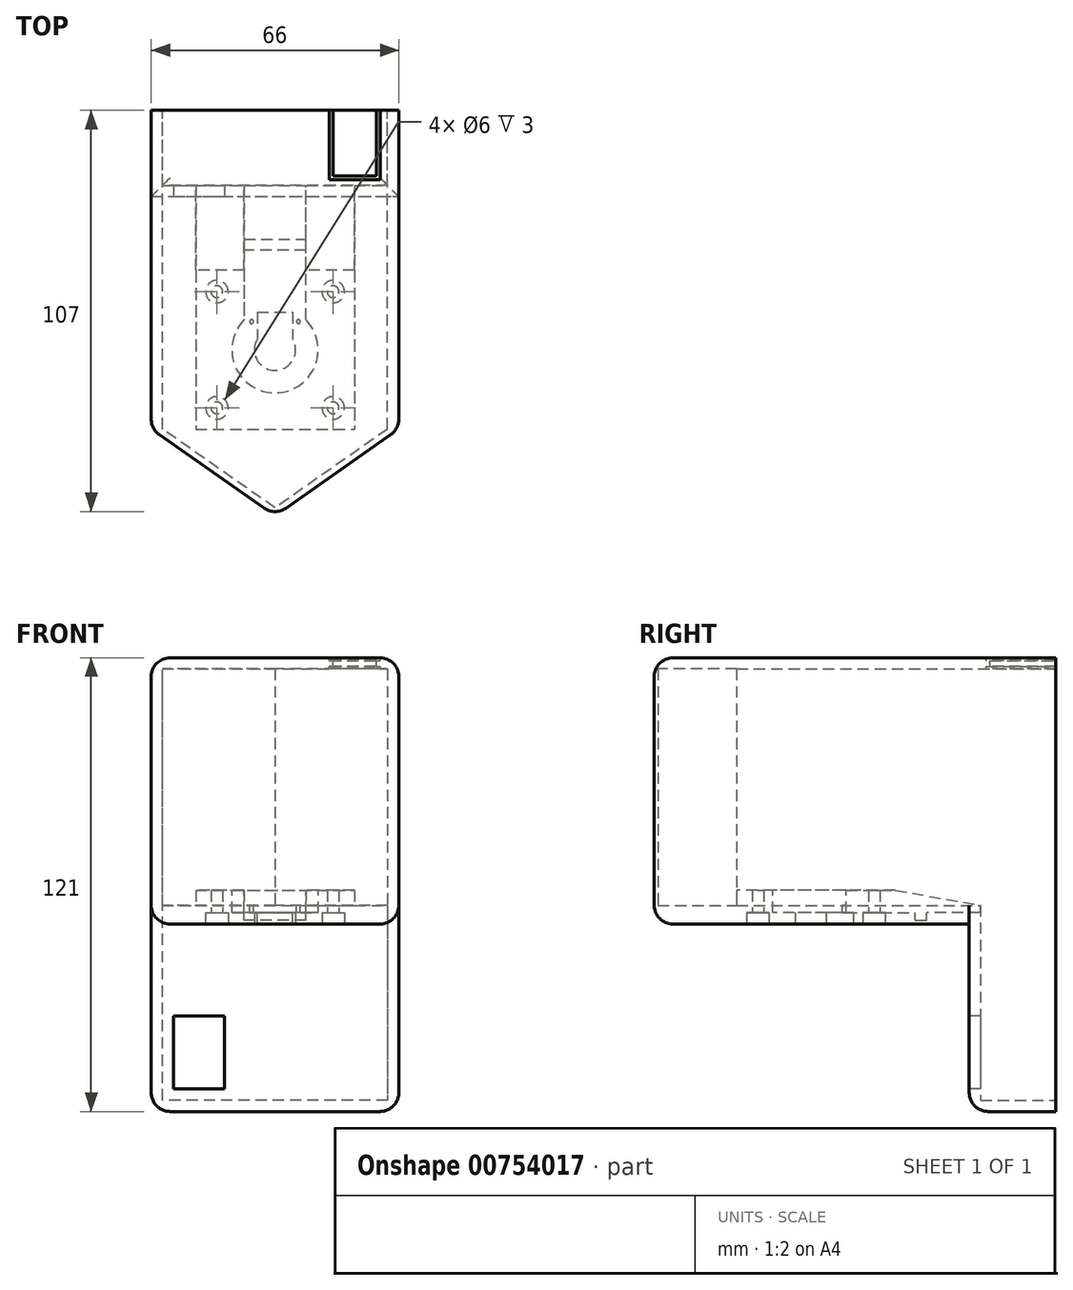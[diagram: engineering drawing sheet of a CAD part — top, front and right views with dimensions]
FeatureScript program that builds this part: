
annotation { "Feature Type Name" : "Feature", "Feature Type Description" : "" }
export const myFeature = defineFeature(function(context is Context, id is Id, definition is map)
    precondition{}
    {
        {
            var Q0;
            Q0=qCreatedBy(makeId("Front.planeOp"),FACE);
            var sketch = newSketch(context, id + "F0", { "sketchPlane" : qUnion([Q0])});
            skLineSegment(sketch, "E0", {"start": v(-33, -60.5) * mm, "end": v(33, -60.5) * mm});
            skLineSegment(sketch, "E1", {"start": v(33, -60.5) * mm, "end": v(33, 60.5) * mm});
            skLineSegment(sketch, "E2", {"start": v(33, 60.5) * mm, "end": v(-33, 60.5) * mm});
            skLineSegment(sketch, "E3", {"start": v(-33, 60.5) * mm, "end": v(-33, -60.5) * mm});
            skLineSegment(sketch, "E4", {"start": v(30, 57.5) * mm, "end": v(30, -57.5) * mm});
            skLineSegment(sketch, "E5", {"start": v(30, -57.5) * mm, "end": v(-30, -57.5) * mm});
            skLineSegment(sketch, "E6", {"start": v(-30, -57.5) * mm, "end": v(-30, 57.5) * mm});
            skLineSegment(sketch, "E7", {"start": v(-30, 57.5) * mm, "end": v(30, 57.5) * mm});
            skSolve(sketch);
        }
        {
            var Q0;
            Q0=makeQuery(id+"F0.imprint","IMPRINT",FACE,{"disambiguationData":[TD([[makeQuery(id+"F0.imprint","IMPRINT",EDGE,{"derivedFrom":sQuery(id+"F0.wireOp",EDGE,"E0")}),1.0]])]});
            extrude(context, id + "F1", {"entities" : qUnion([Q0]), "depth" : 20 * mm, "offsetDistance" : 25 * mm});
        }
        {
            var Q0;
            Q0=makeQuery(id+"F1.opExtrude","CAP_FACE",FACE,{"disambiguationData":[OSD([sQuery(id+"F0.wireOp",EDGE,"E0"),sQuery(id+"F0.wireOp",EDGE,"E1"),sQuery(id+"F0.wireOp",EDGE,"E2"),sQuery(id+"F0.wireOp",EDGE,"E3"),sQuery(id+"F0.wireOp",EDGE,"E4"),sQuery(id+"F0.wireOp",EDGE,"E5"),sQuery(id+"F0.wireOp",EDGE,"E6"),sQuery(id+"F0.wireOp",EDGE,"E7")])],"isStart":false});
            var sketch = newSketch(context, id + "F2", { "sketchPlane" : qUnion([Q0])});
            skLineSegment(sketch, "E8", {"start": v(-33, -10.5) * mm, "end": v(33, -10.5) * mm});
            skLineSegment(sketch, "E9", {"start": v(-33, -5.5) * mm, "end": v(33, -5.5) * mm});
            skSolve(sketch);
        }
        {
            var Q0;
            {var subQ5=makeQuery(id+"F1.opExtrude","CAP_EDGE",EDGE,{"disambiguationData":[OSD([sQuery(id+"F0.wireOp",EDGE,"E5")])],"isStart":false});Q0=makeQuery(id+"F2.imprint","IMPRINT",FACE,{"disambiguationData":[TD([[makeQuery(id+"F2.imprint","IMPRINT",EDGE,{"derivedFrom":subQ5}),-1.0]])]});}
            var Q1;
            {var subQ0=makeQuery(id+"F1.opExtrude","CAP_EDGE",EDGE,{"disambiguationData":[OSD([sQuery(id+"F0.wireOp",EDGE,"E0")])],"isStart":false});Q1=makeQuery(id+"F2.imprint","IMPRINT",FACE,{"disambiguationData":[TD([[makeQuery(id+"F2.imprint","IMPRINT",EDGE,{"derivedFrom":subQ0}),1.0]])]});}
            extrude(context, id + "F3", {"entities" : qUnion([Q0, Q1]), "operationType" : NewBodyOperationType.ADD, "depth" : 3 * mm, "offsetDistance" : 25 * mm});
        }
        {
            var Q0;
            {var subQ0=sQuery(id+"F2.wireOp",EDGE,"E8");var subQ1=makeQuery(id+"F1.opExtrude","CAP_EDGE",EDGE,{"disambiguationData":[OSD([sQuery(id+"F0.wireOp",EDGE,"E6")])],"isStart":false});var subQ2=makeQuery(id+"F2.imprint","INTERSECT",VERTEX,{"derivedFrom":[subQ1,subQ0]});Q0=makeQuery(id+"F2.imprint","IMPRINT",FACE,{"disambiguationData":[TD([[makeQuery(id+"F2.imprint","IMPRINT",EDGE,{"disambiguationData":[TD([[subQ2,-1.0]])],"derivedFrom":subQ0}),1.0]])]});}
            var Q1;
            {var subQ4=makeQuery(id+"F1.opExtrude","CAP_EDGE",EDGE,{"disambiguationData":[OSD([sQuery(id+"F0.wireOp",EDGE,"E2")])],"isStart":false});Q1=makeQuery(id+"F2.imprint","IMPRINT",FACE,{"disambiguationData":[TD([[makeQuery(id+"F2.imprint","IMPRINT",EDGE,{"derivedFrom":subQ4}),1.0]])]});}
            var Q2;
            {var subQ0=sQuery(id+"F2.wireOp",EDGE,"E8");var subQ1=makeQuery(id+"F1.opExtrude","CAP_EDGE",EDGE,{"disambiguationData":[OSD([sQuery(id+"F0.wireOp",EDGE,"E1")])],"isStart":false});var subQ2=makeQuery(id+"F2.imprint","INTERSECT",VERTEX,{"derivedFrom":[subQ1,subQ0]});Q2=makeQuery(id+"F2.imprint","IMPRINT",FACE,{"disambiguationData":[TD([[makeQuery(id+"F2.imprint","IMPRINT",EDGE,{"disambiguationData":[TD([[subQ2,1.0]])],"derivedFrom":subQ0}),1.0]])]});}
            var Q3;
            {var subQ0=sQuery(id+"F2.wireOp",EDGE,"E8");var subQ1=makeQuery(id+"F1.opExtrude","CAP_EDGE",EDGE,{"disambiguationData":[OSD([sQuery(id+"F0.wireOp",EDGE,"E3")])],"isStart":false});var subQ2=makeQuery(id+"F2.imprint","INTERSECT",VERTEX,{"derivedFrom":[subQ1,subQ0]});Q3=makeQuery(id+"F2.imprint","IMPRINT",FACE,{"disambiguationData":[TD([[makeQuery(id+"F2.imprint","IMPRINT",EDGE,{"disambiguationData":[TD([[subQ2,-1.0]])],"derivedFrom":subQ0}),1.0]])]});}
            extrude(context, id + "F4", {"entities" : qUnion([Q0, Q1, Q2, Q3]), "operationType" : NewBodyOperationType.ADD, "depth" : 65 * mm, "offsetDistance" : 25 * mm});
        }
        {
            var Q0;
            Q0=makeQuery(id+"F4.opExtrude","SWEPT_FACE",FACE,{"disambiguationData":[OSD([sQuery(id+"F2.wireOp",EDGE,"E8")])]});
            var sketch = newSketch(context, id + "F5", { "sketchPlane" : qUnion([Q0])});
            skCircle(sketch, "E10", {"center": v(0, 63.85) * mm, "radius": 5.5 * mm});
            skPoint(sketch, "E11", {"position": v(15.5, 79.35) * mm});
            skPoint(sketch, "E12", {"position": v(-15.5, 79.35) * mm});
            skPoint(sketch, "E13", {"position": v(-15.5, 48.35) * mm});
            skPoint(sketch, "E14", {"position": v(15.5, 48.35) * mm});
            skLineSegment(sketch, "E15.bottom", {"start": v(21.15, 42.7) * mm, "end": v(-21.15, 42.7) * mm, "construction": true});
            skLineSegment(sketch, "E15.top", {"start": v(21.15, 85) * mm, "end": v(-21.15, 85) * mm, "construction": true});
            skLineSegment(sketch, "E15.left", {"start": v(21.15, 42.7) * mm, "end": v(21.15, 85) * mm, "construction": true});
            skLineSegment(sketch, "E15.right", {"start": v(-21.15, 42.7) * mm, "end": v(-21.15, 85) * mm, "construction": true});
            skLineSegment(sketch, "E16", {"start": v(3.4, 63.85) * mm, "end": v(-2.9, 63.85) * mm, "construction": true});
            skSolve(sketch);
        }
        {
            var Q0;
            Q0=sQuery(id+"F5.wireOp",VERTEX,"E12");
            var Q1;
            Q1=sQuery(id+"F5.wireOp",VERTEX,"E13");
            var Q2;
            Q2=sQuery(id+"F5.wireOp",VERTEX,"E14");
            var Q3;
            Q3=sQuery(id+"F5.wireOp",VERTEX,"E11");
            var Q4;
            Q4=makeQuery(id+"F1.opExtrude","SWEPT_BODY",BODY,{"disambiguationData":[OSD([sQuery(id+"F0.wireOp",EDGE,"E0"),sQuery(id+"F0.wireOp",EDGE,"E1"),sQuery(id+"F0.wireOp",EDGE,"E2"),sQuery(id+"F0.wireOp",EDGE,"E3"),sQuery(id+"F0.wireOp",EDGE,"E4"),sQuery(id+"F0.wireOp",EDGE,"E5"),sQuery(id+"F0.wireOp",EDGE,"E6"),sQuery(id+"F0.wireOp",EDGE,"E7")])]});
            hole(context, id + "F6", {"style" : HoleStyle.C_BORE, "endStyle" : HoleEndStyle.BLIND, "holeDiameter" : 3.1 * mm, "cBoreDiameter" : 6 * mm, "cBoreDepth" : 3 * mm, "majorDiameter" : 5 * mm, "holeDepth" : 12 * mm, "isTappedThrough" : true, "tappedDepth" : 12 * mm, "tapClearance" : 3, "locations" : qUnion([Q0, Q1, Q2, Q3]), "scope" : qUnion([Q4])});
        }
        {
            var Q0;
            Q0=makeQuery(id+"F5.imprint","IMPRINT",FACE,{"disambiguationData":[TD([[makeQuery(id+"F5.imprint","IMPRINT",EDGE,{"derivedFrom":sQuery(id+"F5.wireOp",EDGE,"E10")}),1.0]])]});
            extrude(context, id + "F7", {"entities" : qUnion([Q0]), "operationType" : NewBodyOperationType.REMOVE, "oppositeDirection" : true, "depth" : 3 * mm, "offsetDistance" : 25 * mm});
        }
        {
            var Q0;
            Q0=makeQuery(id+"F3.opExtrude","CAP_FACE",FACE,{"disambiguationData":[OSD([sQuery(id+"F0.wireOp",EDGE,"E0"),sQuery(id+"F0.wireOp",EDGE,"E1"),sQuery(id+"F0.wireOp",EDGE,"E3"),sQuery(id+"F2.wireOp",EDGE,"E8")])],"isStart":false});
            var sketch = newSketch(context, id + "F8", { "sketchPlane" : qUnion([Q0])});
            skLineSegment(sketch, "E17.bottom", {"start": v(-27, -35) * mm, "end": v(-13.5, -35) * mm});
            skLineSegment(sketch, "E17.top", {"start": v(-27, -54.5) * mm, "end": v(-13.5, -54.5) * mm});
            skLineSegment(sketch, "E17.left", {"start": v(-27, -35) * mm, "end": v(-27, -54.5) * mm});
            skLineSegment(sketch, "E17.right", {"start": v(-13.5, -35) * mm, "end": v(-13.5, -54.5) * mm});
            skSolve(sketch);
        }
        {
            var Q0;
            Q0=makeQuery(id+"F8.imprint","IMPRINT",FACE,{"disambiguationData":[TD([[makeQuery(id+"F8.imprint","IMPRINT",EDGE,{"derivedFrom":sQuery(id+"F8.wireOp",EDGE,"E17.bottom")}),-1.0]])]});
            extrude(context, id + "F9", {"entities" : qUnion([Q0]), "operationType" : NewBodyOperationType.REMOVE, "oppositeDirection" : true, "depth" : 3 * mm, "offsetDistance" : 25 * mm});
        }
        {
            var Q0;
            {var subQ0=sQuery(id+"F0.wireOp",EDGE,"E2");Q0=makeQuery(id+"F4.boolean.opBoolean","MERGE",FACE,{"derivedFrom":[makeQuery(id+"F1.opExtrude","SWEPT_FACE",FACE,{"disambiguationData":[OSD([subQ0])]}),makeQuery(id+"F4.opExtrude","SWEPT_FACE",FACE,{"disambiguationData":[OSD([subQ0])]})]});}
            var sketch = newSketch(context, id + "F10", { "sketchPlane" : qUnion([Q0])});
            skLineSegment(sketch, "E18.bottom", {"start": v(28, -3) * mm, "end": v(14.5, -3) * mm});
            skLineSegment(sketch, "E18.top", {"start": v(28, -18.5) * mm, "end": v(14.5, -18.5) * mm});
            skLineSegment(sketch, "E18.left", {"start": v(28, -3) * mm, "end": v(28, -18.5) * mm});
            skLineSegment(sketch, "E18.right", {"start": v(14.5, -3) * mm, "end": v(14.5, -18.5) * mm});
            skSolve(sketch);
        }
        {
            var Q0;
            Q0=makeQuery(id+"F10.imprint","IMPRINT",FACE,{"disambiguationData":[TD([[makeQuery(id+"F10.imprint","IMPRINT",EDGE,{"derivedFrom":sQuery(id+"F10.wireOp",EDGE,"E18.bottom")}),1.0]])]});
            extrude(context, id + "F11", {"entities" : qUnion([Q0]), "operationType" : NewBodyOperationType.REMOVE, "oppositeDirection" : true, "depth" : 3 * mm, "offsetDistance" : 25 * mm});
        }
        {
            var Q0;
            Q0=makeQuery(id+"F4.opExtrude","SWEPT_FACE",FACE,{"disambiguationData":[OSD([sQuery(id+"F2.wireOp",EDGE,"E9")])]});
            var sketch = newSketch(context, id + "F12", { "sketchPlane" : qUnion([Q0])});
            skLineSegment(sketch, "E19", {"start": v(8.25, -55.84) * mm, "end": v(8.25, -20) * mm});
            skLineSegment(sketch, "E20", {"start": v(-8.25, -20) * mm, "end": v(-8.25, -55.84) * mm});
            skPoint(sketch, "E21", {"position": v(15.5, -48.35) * mm});
            skPoint(sketch, "E22", {"position": v(-15.5, -48.35) * mm});
            skCircle(sketch, "E23", {"center": v(0, -63.85) * mm, "radius": 11.5 * mm});
            skPoint(sketch, "E24", {"position": v(-6.25, -56.35) * mm});
            skPoint(sketch, "E25", {"position": v(6.25, -56.35) * mm});
            skCircle(sketch, "E26", {"center": v(6.25, -56.35) * mm, "radius": 0.5 * mm});
            skCircle(sketch, "E27", {"center": v(-6.25, -56.35) * mm, "radius": 0.5 * mm});
            skLineSegment(sketch, "E28", {"start": v(-8.25, -55.84) * mm, "end": v(-8.25, -58.35) * mm, "construction": true});
            skLineSegment(sketch, "E29", {"start": v(-8.25, -58.35) * mm, "end": v(-4.75, -58.35) * mm, "construction": true});
            skLineSegment(sketch, "E30", {"start": v(-4.75, -53.85) * mm, "end": v(4.75, -53.85) * mm});
            skLineSegment(sketch, "E31", {"start": v(4.75, -58.35) * mm, "end": v(8.25, -58.35) * mm, "construction": true});
            skLineSegment(sketch, "E32", {"start": v(8.25, -58.35) * mm, "end": v(8.25, -55.84) * mm, "construction": true});
            skCircle(sketch, "E33", {"center": v(0, -63.85) * mm, "radius": 5.5 * mm});
            skLineSegment(sketch, "E34", {"start": v(4.75, -53.85) * mm, "end": v(4.75, -61.08) * mm});
            skLineSegment(sketch, "E35", {"start": v(-4.75, -53.85) * mm, "end": v(-4.75, -61.08) * mm});
            skLineSegment(sketch, "E36.bottom", {"start": v(21.15, -42.7) * mm, "end": v(-21.15, -42.7) * mm});
            skLineSegment(sketch, "E36.top", {"start": v(21.15, -85) * mm, "end": v(-21.15, -85) * mm});
            skLineSegment(sketch, "E36.left", {"start": v(21.15, -42.7) * mm, "end": v(21.15, -85) * mm});
            skLineSegment(sketch, "E36.right", {"start": v(-21.15, -42.7) * mm, "end": v(-21.15, -85) * mm});
            skSolve(sketch);
        }
        {
            var Q0;
            Q0=makeQuery(id+"F12.imprint","IMPRINT",FACE,{"disambiguationData":[TD([[makeQuery(id+"F12.imprint","IMPRINT",EDGE,{"derivedFrom":sQuery(id+"F12.wireOp",EDGE,"E23")}),1.0]])]});
            var Q1;
            {var subQ0=sQuery(id+"F12.wireOp",EDGE,"E19");var subQ1=makeQuery(id+"F4.opExtrude","CAP_EDGE",EDGE,{"disambiguationData":[OSD([sQuery(id+"F2.wireOp",EDGE,"E9")])],"isStart":true});var subQ2=makeQuery(id+"F12.imprint","INTERSECT",VERTEX,{"derivedFrom":[subQ1,subQ0]});Q1=makeQuery(id+"F12.imprint","IMPRINT",FACE,{"disambiguationData":[TD([[makeQuery(id+"F12.imprint","IMPRINT",EDGE,{"disambiguationData":[TD([[subQ2,1.0]])],"derivedFrom":subQ0}),1.0]])]});}
            var Q2;
            {var subQ0=sQuery(id+"F12.wireOp",EDGE,"t75Lk9a1-lg42-faZ2-Xwdc-VcRS5GfcYv8D");var subQ1=sQuery(id+"F12.wireOp",EDGE,"E23");var subQ2=makeQuery(id+"F12.imprint","INTERSECT",VERTEX,{"derivedFrom":[subQ1,subQ0]});Q2=makeQuery(id+"F12.imprint","IMPRINT",FACE,{"disambiguationData":[TD([[makeQuery(id+"F12.imprint","IMPRINT",EDGE,{"disambiguationData":[TD([[subQ2,-1.0]])],"derivedFrom":subQ1}),-1.0]])]});}
            var Q3;
            {var subQ0=sQuery(id+"F12.wireOp",EDGE,"E30");var subQ1=sQuery(id+"F12.wireOp",EDGE,"E23");var subQ2=makeQuery(id+"F12.imprint","INTERSECT",VERTEX,{"disambiguationData":[OD(0.0)],"derivedFrom":[subQ1,subQ0]});Q3=makeQuery(id+"F12.imprint","IMPRINT",FACE,{"disambiguationData":[TD([[makeQuery(id+"F12.imprint","IMPRINT",EDGE,{"disambiguationData":[TD([[subQ2,-1.0]])],"derivedFrom":subQ1}),1.0]])]});}
            var Q4;
            {var subQ0=sQuery(id+"F12.wireOp",EDGE,"E33");var subQ1=makeQuery(id+"F12.imprint","INTERSECT",VERTEX,{"derivedFrom":[subQ0,sQuery(id+"F12.wireOp",EDGE,"E34")]});Q4=makeQuery(id+"F12.imprint","IMPRINT",FACE,{"disambiguationData":[TD([[makeQuery(id+"F12.imprint","IMPRINT",EDGE,{"disambiguationData":[TD([[subQ1,-1.0]])],"derivedFrom":subQ0}),1.0]])]});}
            extrude(context, id + "F13", {"entities" : qUnion([Q0, Q1, Q2, Q3, Q4]), "operationType" : NewBodyOperationType.REMOVE, "oppositeDirection" : true, "depth" : 2 * mm, "offsetDistance" : 25 * mm});
        }
        {
            var Q0;
            Q0=makeQuery(id+"F12.imprint","IMPRINT",FACE,{"disambiguationData":[TD([[makeQuery(id+"F12.imprint","IMPRINT",EDGE,{"derivedFrom":sQuery(id+"F12.wireOp",EDGE,"E30")}),-1.0]])]});
            extrude(context, id + "F14", {"entities" : qUnion([Q0]), "operationType" : NewBodyOperationType.REMOVE, "oppositeDirection" : true, "depth" : 25 * mm, "offsetDistance" : 25 * mm});
        }
        {
            var Q0;
            Q0=makeQuery(id+"F13.boolean.opBoolean","COPY",FACE,{"derivedFrom":makeQuery(id+"F13.opExtrude","CAP_FACE",FACE,{"disambiguationData":[OSD([sQuery(id+"F2.wireOp",EDGE,"E9"),sQuery(id+"F12.wireOp",EDGE,"E19"),sQuery(id+"F12.wireOp",EDGE,"E20"),sQuery(id+"F12.wireOp",EDGE,"E23"),sQuery(id+"F12.wireOp",EDGE,"E26"),sQuery(id+"F12.wireOp",EDGE,"E27"),sQuery(id+"F12.wireOp",EDGE,"E30"),sQuery(id+"F12.wireOp",EDGE,"E33"),sQuery(id+"F12.wireOp",EDGE,"E34"),sQuery(id+"F12.wireOp",EDGE,"E35")])],"isStart":false})});
            var sketch = newSketch(context, id + "F15", { "sketchPlane" : qUnion([Q0])});
            skLineSegment(sketch, "E37", {"start": v(8.25, -37.35) * mm, "end": v(-8.25, -37.35) * mm});
            skLineSegment(sketch, "E38", {"start": v(-8.25, -34.35) * mm, "end": v(8.25, -34.35) * mm});
            skLineSegment(sketch, "E39", {"start": v(-8.25, -34.35) * mm, "end": v(-8.25, -37.35) * mm});
            skLineSegment(sketch, "E40", {"start": v(8.25, -34.35) * mm, "end": v(8.25, -37.35) * mm});
            skSolve(sketch);
        }
        {
            var Q0;
            Q0=makeQuery(id+"F15.imprint","IMPRINT",FACE,{"disambiguationData":[TD([[makeQuery(id+"F15.imprint","IMPRINT",EDGE,{"derivedFrom":sQuery(id+"F15.wireOp",EDGE,"E37")}),-1.0]])]});
            extrude(context, id + "F16", {"entities" : qUnion([Q0]), "operationType" : NewBodyOperationType.REMOVE, "oppositeDirection" : true, "depth" : 2 * mm, "offsetDistance" : 25 * mm});
        }
        {
            var Q0;
            Q0=makeQuery(id+"F4.opExtrude","SWEPT_FACE",FACE,{"disambiguationData":[OSD([sQuery(id+"F2.wireOp",EDGE,"E8")])]});
            var sketch = newSketch(context, id + "F17", { "sketchPlane" : qUnion([Q0])});
            skLineSegment(sketch, "E41", {"start": v(0, 108.1) * mm, "end": v(-33, 85) * mm});
            skPoint(sketch, "E41.startSnap0", {"position": v(0, 85) * mm});
            skLineSegment(sketch, "E42", {"start": v(0, 108.1) * mm, "end": v(33, 85) * mm});
            skSolve(sketch);
        }
        {
            var Q0;
            Q0=makeQuery(id+"F17.imprint","IMPRINT",FACE,{"disambiguationData":[TD([[makeQuery(id+"F17.imprint","IMPRINT",EDGE,{"derivedFrom":sQuery(id+"F17.wireOp",EDGE,"E41")}),1.0]])]});
            extrude(context, id + "F18", {"entities" : qUnion([Q0]), "operationType" : NewBodyOperationType.ADD, "oppositeDirection" : true, "depth" : 5 * mm, "offsetDistance" : 25 * mm});
        }
        {
            var Q0;
            {var subQ0=sQuery(id+"F2.wireOp",EDGE,"E8");var subQ2=sQuery(id+"F2.wireOp",EDGE,"E9");var subQ4=sQuery(id+"F0.wireOp",EDGE,"E4");Q0=makeQuery(id+"F18.boolean.opBoolean","MERGE",FACE,{"derivedFrom":[makeQuery(id+"F13.boolean.opBoolean","SPLIT",FACE,{"disambiguationData":[TD([makeQuery(id+"F1.opExtrude","SWEPT_FACE",FACE,{"disambiguationData":[OSD([subQ4])]})])],"derivedFrom":makeQuery(id+"F4.opExtrude","SWEPT_FACE",FACE,{"disambiguationData":[OSD([subQ2])]})}),makeQuery(id+"F18.opExtrude","CAP_FACE",FACE,{"disambiguationData":[OSD([subQ0,sQuery(id+"F17.wireOp",EDGE,"E41"),sQuery(id+"F17.wireOp",EDGE,"E42")])],"isStart":false})]});}
            var sketch = newSketch(context, id + "F19", { "sketchPlane" : qUnion([Q0])});
            skLineSegment(sketch, "E43", {"start": v(30, -85) * mm, "end": v(0, -106) * mm});
            skLineSegment(sketch, "E44", {"start": v(0, -106) * mm, "end": v(-30, -85) * mm});
            skSolve(sketch);
        }
        {
            var Q0;
            {var subQ0=sQuery(id+"F0.wireOp",EDGE,"E2");Q0=makeQuery(id+"F4.boolean.opBoolean","MERGE",FACE,{"derivedFrom":[makeQuery(id+"F1.opExtrude","SWEPT_FACE",FACE,{"disambiguationData":[OSD([subQ0])]}),makeQuery(id+"F4.opExtrude","SWEPT_FACE",FACE,{"disambiguationData":[OSD([subQ0])]})]});}
            var sketch = newSketch(context, id + "F20", { "sketchPlane" : qUnion([Q0])});
            skLineSegment(sketch, "E45", {"start": v(33, -85) * mm, "end": v(0, -108.1) * mm});
            skLineSegment(sketch, "E46", {"start": v(0, -108.1) * mm, "end": v(-33, -85) * mm});
            skSolve(sketch);
        }
        {
            var Q0;
            Q0=makeQuery(id+"F20.imprint","IMPRINT",FACE,{"disambiguationData":[TD([[makeQuery(id+"F20.imprint","IMPRINT",EDGE,{"derivedFrom":sQuery(id+"F20.wireOp",EDGE,"E45")}),-1.0]])]});
            extrude(context, id + "F21", {"entities" : qUnion([Q0]), "operationType" : NewBodyOperationType.ADD, "oppositeDirection" : true, "depth" : 3 * mm, "offsetDistance" : 25 * mm});
        }
        {
            var Q0;
            Q0=makeQuery(id+"F19.imprint","IMPRINT",FACE,{"disambiguationData":[TD([[makeQuery(id+"F19.imprint","IMPRINT",EDGE,{"derivedFrom":sQuery(id+"F19.wireOp",EDGE,"E43")}),1.0]])]});
            extrude(context, id + "F22", {"entities" : qUnion([Q0]), "operationType" : NewBodyOperationType.ADD, "depth" : 63 * mm, "offsetDistance" : 25 * mm});
        }
        {
            var Q0;
            Q0=makeQuery(id+"F18.opExtrude","CAP_EDGE",EDGE,{"disambiguationData":[OSD([sQuery(id+"F17.wireOp",EDGE,"E42")])],"isStart":true});
            var Q1;
            Q1=makeQuery(id+"F18.opExtrude","CAP_EDGE",EDGE,{"disambiguationData":[OSD([sQuery(id+"F17.wireOp",EDGE,"E41")])],"isStart":true});
            var Q2;
            {var subQ0=sQuery(id+"F17.wireOp",EDGE,"E42");var subQ1=sQuery(id+"F17.wireOp",EDGE,"E41");Q2=makeQuery(id+"F22.boolean.opBoolean","MERGE",EDGE,{"derivedFrom":[makeQuery(id+"F18.opExtrude","SWEPT_EDGE",EDGE,{"disambiguationData":[OSD([subQ1,subQ0])]}),makeQuery(id+"F21.opExtrude","SWEPT_EDGE",EDGE,{"disambiguationData":[OSD([sQuery(id+"F20.wireOp",EDGE,"E45"),sQuery(id+"F20.wireOp",EDGE,"E46")])]}),makeQuery(id+"F22.opExtrude","SWEPT_EDGE",EDGE,{"disambiguationData":[OSD([subQ1,subQ0])]})]});}
            var Q3;
            Q3=makeQuery(id+"F3.opExtrude","CAP_EDGE",EDGE,{"disambiguationData":[OSD([sQuery(id+"F2.wireOp",EDGE,"E8")])],"isStart":false});
            var Q4;
            Q4=makeQuery(id+"F4.opExtrude","SWEPT_EDGE",EDGE,{"disambiguationData":[OSD([sQuery(id+"F0.wireOp",EDGE,"E1"),sQuery(id+"F2.wireOp",EDGE,"E8")])]});
            var Q5;
            {var subQ0=sQuery(id+"F17.wireOp",EDGE,"E42");var subQ1=sQuery(id+"F2.wireOp",EDGE,"E8");var subQ2=sQuery(id+"F0.wireOp",EDGE,"E1");var subQ3=makeQuery(id+"F4.opExtrude","CAP_EDGE",EDGE,{"disambiguationData":[OSD([subQ2])],"isStart":false});var subQ4=makeQuery(id+"F18.boolean.opBoolean","SPLIT",EDGE,{"derivedFrom":subQ3});Q5=makeQuery(id+"F22.boolean.opBoolean","MERGE",EDGE,{"derivedFrom":[makeQuery(id+"F18.boolean.opBoolean","MERGE",EDGE,{"derivedFrom":[subQ3,makeQuery(id+"F18.opExtrude","SWEPT_EDGE",EDGE,{"disambiguationData":[OSD([subQ2,subQ1,subQ0])]})]}),makeQuery(id+"F21.boolean.opBoolean","MERGE",EDGE,{"derivedFrom":[subQ4,makeQuery(id+"F21.opExtrude","SWEPT_EDGE",EDGE,{"disambiguationData":[OSD([subQ2,sQuery(id+"F0.wireOp",EDGE,"E2"),sQuery(id+"F20.wireOp",EDGE,"E45")])]})]}),makeQuery(id+"F21.boolean.opBoolean","SPLIT",EDGE,{"derivedFrom":subQ4}),makeQuery(id+"F22.opExtrude","SWEPT_EDGE",EDGE,{"disambiguationData":[OSD([subQ1,subQ0])]})]});}
            var Q6;
            Q6=makeQuery(id+"F4.opExtrude","SWEPT_EDGE",EDGE,{"disambiguationData":[OSD([sQuery(id+"F0.wireOp",EDGE,"E3"),sQuery(id+"F2.wireOp",EDGE,"E8")])]});
            var Q7;
            {var subQ0=sQuery(id+"F17.wireOp",EDGE,"E41");var subQ1=sQuery(id+"F2.wireOp",EDGE,"E8");var subQ2=sQuery(id+"F0.wireOp",EDGE,"E3");var subQ3=makeQuery(id+"F4.opExtrude","CAP_EDGE",EDGE,{"disambiguationData":[OSD([subQ2])],"isStart":false});var subQ4=makeQuery(id+"F18.boolean.opBoolean","SPLIT",EDGE,{"derivedFrom":subQ3});Q7=makeQuery(id+"F22.boolean.opBoolean","MERGE",EDGE,{"derivedFrom":[makeQuery(id+"F18.boolean.opBoolean","MERGE",EDGE,{"derivedFrom":[subQ3,makeQuery(id+"F18.opExtrude","SWEPT_EDGE",EDGE,{"disambiguationData":[OSD([subQ2,subQ1,subQ0])]})]}),makeQuery(id+"F21.boolean.opBoolean","MERGE",EDGE,{"derivedFrom":[subQ4,makeQuery(id+"F21.opExtrude","SWEPT_EDGE",EDGE,{"disambiguationData":[OSD([sQuery(id+"F0.wireOp",EDGE,"E2"),subQ2,sQuery(id+"F20.wireOp",EDGE,"E46")])]})]}),makeQuery(id+"F21.boolean.opBoolean","SPLIT",EDGE,{"derivedFrom":subQ4}),makeQuery(id+"F22.opExtrude","SWEPT_EDGE",EDGE,{"disambiguationData":[OSD([subQ1,subQ0])]})]});}
            var Q8;
            Q8=makeQuery(id+"F21.opExtrude","CAP_EDGE",EDGE,{"disambiguationData":[OSD([sQuery(id+"F20.wireOp",EDGE,"E46")])],"isStart":true});
            var Q9;
            {var subQ0=sQuery(id+"F0.wireOp",EDGE,"E3");var subQ1=sQuery(id+"F0.wireOp",EDGE,"E2");Q9=makeQuery(id+"F4.boolean.opBoolean","MERGE",EDGE,{"derivedFrom":[makeQuery(id+"F1.opExtrude","SWEPT_EDGE",EDGE,{"disambiguationData":[OSD([subQ1,subQ0])]}),makeQuery(id+"F4.opExtrude","SWEPT_EDGE",EDGE,{"disambiguationData":[OSD([subQ1,subQ0])]})]});}
            var Q10;
            {var subQ0=sQuery(id+"F0.wireOp",EDGE,"E2");var subQ1=sQuery(id+"F0.wireOp",EDGE,"E1");Q10=makeQuery(id+"F4.boolean.opBoolean","MERGE",EDGE,{"derivedFrom":[makeQuery(id+"F1.opExtrude","SWEPT_EDGE",EDGE,{"disambiguationData":[OSD([subQ1,subQ0])]}),makeQuery(id+"F4.opExtrude","SWEPT_EDGE",EDGE,{"disambiguationData":[OSD([subQ1,subQ0])]})]});}
            var Q11;
            Q11=makeQuery(id+"F3.opExtrude","CAP_EDGE",EDGE,{"disambiguationData":[OSD([sQuery(id+"F0.wireOp",EDGE,"E0")])],"isStart":false});
            var Q12;
            {var subQ0=sQuery(id+"F0.wireOp",EDGE,"E3");var subQ1=sQuery(id+"F0.wireOp",EDGE,"E0");Q12=makeQuery(id+"F3.boolean.opBoolean","MERGE",EDGE,{"derivedFrom":[makeQuery(id+"F1.opExtrude","SWEPT_EDGE",EDGE,{"disambiguationData":[OSD([subQ1,subQ0])]}),makeQuery(id+"F3.opExtrude","SWEPT_EDGE",EDGE,{"disambiguationData":[OSD([subQ1,subQ0])]})]});}
            var Q13;
            {var subQ0=sQuery(id+"F0.wireOp",EDGE,"E1");var subQ1=sQuery(id+"F0.wireOp",EDGE,"E0");Q13=makeQuery(id+"F3.boolean.opBoolean","MERGE",EDGE,{"derivedFrom":[makeQuery(id+"F1.opExtrude","SWEPT_EDGE",EDGE,{"disambiguationData":[OSD([subQ1,subQ0])]}),makeQuery(id+"F3.opExtrude","SWEPT_EDGE",EDGE,{"disambiguationData":[OSD([subQ1,subQ0])]})]});}
            var Q14;
            Q14=makeQuery(id+"F21.opExtrude","CAP_EDGE",EDGE,{"disambiguationData":[OSD([sQuery(id+"F20.wireOp",EDGE,"E45")])],"isStart":true});
            fillet(context, id + "F23", {"entities" : qUnion([Q0, Q1, Q2, Q3, Q4, Q5, Q6, Q7, Q8, Q9, Q10, Q11, Q12, Q13, Q14]), "radius" : 5 * mm, "tangentPropagation" : true, "allowEdgeOverflow" : false});
        }
        {
            var Q0;
            Q0=makeQuery(id+"F12.imprint","IMPRINT",FACE,{"disambiguationData":[TD([[makeQuery(id+"F12.imprint","IMPRINT",EDGE,{"derivedFrom":sQuery(id+"F12.wireOp",EDGE,"E36.top")}),1.0]])]});
            extrude(context, id + "F24", {"entities" : qUnion([Q0]), "operationType" : NewBodyOperationType.ADD, "depth" : 4 * mm, "offsetDistance" : 25 * mm});
        }
        {
            var Q0;
            {var subQ0=sQuery(id+"F12.wireOp",EDGE,"E19");Q0=makeQuery(id+"F24.boolean.opBoolean","MERGE",FACE,{"derivedFrom":[makeQuery(id+"F16.boolean.opBoolean","MERGE",FACE,{"derivedFrom":[makeQuery(id+"F13.boolean.opBoolean","COPY",FACE,{"derivedFrom":makeQuery(id+"F13.opExtrude","SWEPT_FACE",FACE,{"disambiguationData":[OSD([subQ0])]})}),makeQuery(id+"F16.opExtrude","SWEPT_FACE",FACE,{"disambiguationData":[OSD([sQuery(id+"F15.wireOp",EDGE,"E40")])]})]}),makeQuery(id+"F24.opExtrude","SWEPT_FACE",FACE,{"disambiguationData":[OSD([subQ0])]})]});}
            var sketch = newSketch(context, id + "F25", { "sketchPlane" : qUnion([Q0])});
            skLineSegment(sketch, "E47", {"start": v(42.7, -1.5) * mm, "end": v(20, -5.5) * mm});
            skSolve(sketch);
        }
        {
            var Q0;
            Q0=makeQuery(id+"F25.imprint","IMPRINT",FACE,{"disambiguationData":[TD([[makeQuery(id+"F25.imprint","IMPRINT",EDGE,{"derivedFrom":sQuery(id+"F25.wireOp",EDGE,"E47")}),1.0]])]});
            extrude(context, id + "F26", {"entities" : qUnion([Q0]), "operationType" : NewBodyOperationType.ADD, "oppositeDirection" : true, "depth" : 12.9 * mm, "offsetDistance" : 25 * mm});
        }
        {
            var Q0;
            {var subQ0=sQuery(id+"F12.wireOp",EDGE,"E20");Q0=makeQuery(id+"F24.boolean.opBoolean","MERGE",FACE,{"derivedFrom":[makeQuery(id+"F16.boolean.opBoolean","MERGE",FACE,{"derivedFrom":[makeQuery(id+"F13.boolean.opBoolean","COPY",FACE,{"derivedFrom":makeQuery(id+"F13.opExtrude","SWEPT_FACE",FACE,{"disambiguationData":[OSD([subQ0])]})}),makeQuery(id+"F16.opExtrude","SWEPT_FACE",FACE,{"disambiguationData":[OSD([sQuery(id+"F15.wireOp",EDGE,"E39")])]})]}),makeQuery(id+"F24.opExtrude","SWEPT_FACE",FACE,{"disambiguationData":[OSD([subQ0])]})]});}
            var sketch = newSketch(context, id + "F27", { "sketchPlane" : qUnion([Q0])});
            skLineSegment(sketch, "E48", {"start": v(-42.7, -1.5) * mm, "end": v(-20, -5.5) * mm});
            skSolve(sketch);
        }
        {
            var Q0;
            Q0=makeQuery(id+"F27.imprint","IMPRINT",FACE,{"disambiguationData":[TD([[makeQuery(id+"F27.imprint","IMPRINT",EDGE,{"derivedFrom":sQuery(id+"F27.wireOp",EDGE,"E48")}),-1.0]])]});
            extrude(context, id + "F28", {"entities" : qUnion([Q0]), "operationType" : NewBodyOperationType.ADD, "oppositeDirection" : true, "depth" : 12.9 * mm, "offsetDistance" : 25 * mm});
        }
        {
            var Q0;
            Q0=makeQuery(id+"F11.boolean.opBoolean","COPY",FACE,{"derivedFrom":makeQuery(id+"F11.opExtrude","SWEPT_FACE",FACE,{"disambiguationData":[OSD([sQuery(id+"F10.wireOp",EDGE,"E18.left")])]})});
            var sketch = newSketch(context, id + "F29", { "sketchPlane" : qUnion([Q0])});
            skLineSegment(sketch, "E49", {"start": v(18.5, 59.75) * mm, "end": v(3, 59.75) * mm});
            skPoint(sketch, "E49.endSnap0", {"position": v(3, 59) * mm});
            skLineSegment(sketch, "E50", {"start": v(3, 58.25) * mm, "end": v(18.5, 58.25) * mm});
            skLineSegment(sketch, "E51", {"start": v(18.5, 59) * mm, "end": v(3, 59) * mm, "construction": true});
            skSolve(sketch);
        }
        {
            var Q0;
            {var subQ0=sQuery(id+"F29.wireOp",EDGE,"E49");Q0=makeQuery(id+"F29.imprint","IMPRINT",FACE,{"disambiguationData":[TD([[makeQuery(id+"F29.imprint","IMPRINT",EDGE,{"derivedFrom":subQ0}),1.0]])]});}
            extrude(context, id + "F30", {"entities" : qUnion([Q0]), "operationType" : NewBodyOperationType.ADD, "depth" : 1 * mm, "offsetDistance" : 25 * mm});
        }
        {
            var Q0;
            Q0=makeQuery(id+"F11.boolean.opBoolean","COPY",FACE,{"derivedFrom":makeQuery(id+"F11.opExtrude","SWEPT_FACE",FACE,{"disambiguationData":[OSD([sQuery(id+"F10.wireOp",EDGE,"E18.right")])]})});
            var sketch = newSketch(context, id + "F31", { "sketchPlane" : qUnion([Q0])});
            skLineSegment(sketch, "E52", {"start": v(-18.5, 59) * mm, "end": v(-3, 59) * mm, "construction": true});
            skLineSegment(sketch, "E53", {"start": v(-3, 59.75) * mm, "end": v(-18.5, 59.75) * mm});
            skLineSegment(sketch, "E54", {"start": v(-18.5, 58.25) * mm, "end": v(-3, 58.25) * mm});
            skSolve(sketch);
        }
        {
            var Q0;
            {var subQ0=sQuery(id+"F31.wireOp",EDGE,"E53");Q0=makeQuery(id+"F31.imprint","IMPRINT",FACE,{"disambiguationData":[TD([[makeQuery(id+"F31.imprint","IMPRINT",EDGE,{"derivedFrom":subQ0}),1.0]])]});}
            extrude(context, id + "F32", {"entities" : qUnion([Q0]), "operationType" : NewBodyOperationType.ADD, "depth" : 1 * mm, "offsetDistance" : 25 * mm});
        }
        {
            var Q0;
            Q0=makeQuery(id+"F11.boolean.opBoolean","COPY",FACE,{"derivedFrom":makeQuery(id+"F11.opExtrude","SWEPT_FACE",FACE,{"disambiguationData":[OSD([sQuery(id+"F10.wireOp",EDGE,"E18.top")])]})});
            var sketch = newSketch(context, id + "F33", { "sketchPlane" : qUnion([Q0])});
            skLineSegment(sketch, "E55", {"start": v(-27, 59.75) * mm, "end": v(-15.5, 59.75) * mm});
            skLineSegment(sketch, "E56", {"start": v(-27, 58.25) * mm, "end": v(-15.5, 58.25) * mm});
            skSolve(sketch);
        }
        {
            var Q0;
            Q0=makeQuery(id+"F33.imprint","IMPRINT",FACE,{"disambiguationData":[TD([[makeQuery(id+"F33.imprint","IMPRINT",EDGE,{"derivedFrom":sQuery(id+"F33.wireOp",EDGE,"E55")}),-1.0]])]});
            extrude(context, id + "F34", {"entities" : qUnion([Q0]), "operationType" : NewBodyOperationType.ADD, "depth" : 1 * mm, "offsetDistance" : 25 * mm});
        }
        {
            var Q0;
            Q0=makeQuery(id+"F11.boolean.opBoolean","COPY",FACE,{"derivedFrom":makeQuery(id+"F11.opExtrude","SWEPT_FACE",FACE,{"disambiguationData":[OSD([sQuery(id+"F10.wireOp",EDGE,"E18.bottom")])]})});
            extrude(context, id + "F35", {"entities" : qUnion([Q0]), "operationType" : NewBodyOperationType.REMOVE, "oppositeDirection" : true, "depth" : 25 * mm, "offsetDistance" : 25 * mm});
        }
    });
